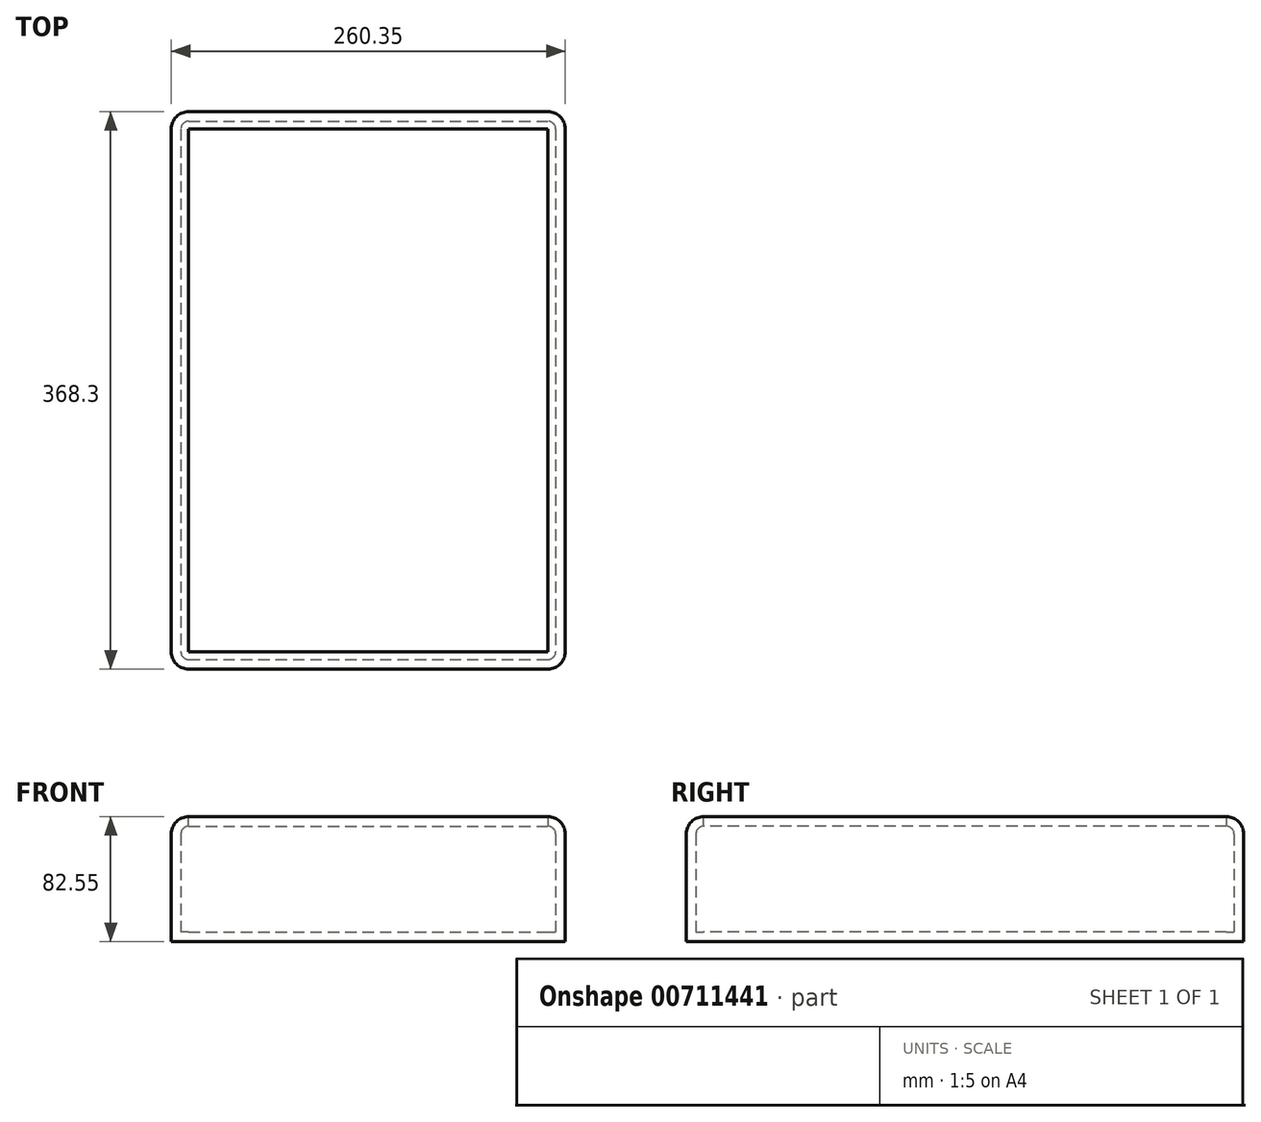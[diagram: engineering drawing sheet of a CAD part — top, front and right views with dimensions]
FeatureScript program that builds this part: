
annotation { "Feature Type Name" : "Feature", "Feature Type Description" : "" }
export const myFeature = defineFeature(function(context is Context, id is Id, definition is map)
    precondition{}
    {
        {
            var Q0;
            Q0=qCreatedBy(makeId("Top.planeOp"),FACE);
            var sketch = newSketch(context, id + "F0", { "sketchPlane" : qUnion([Q0])});
            skLineSegment(sketch, "E0.bottom", {"start": v(-252.64, 180.78) * mm, "end": v(-5, 180.78) * mm});
            skLineSegment(sketch, "E0.top", {"start": v(-252.64, -174.82) * mm, "end": v(-5, -174.82) * mm});
            skLineSegment(sketch, "E0.left", {"start": v(-252.64, 180.78) * mm, "end": v(-252.64, -174.82) * mm});
            skLineSegment(sketch, "E0.right", {"start": v(-5, 180.78) * mm, "end": v(-5, -174.82) * mm});
            skSolve(sketch);
        }
        {
            var Q0;
            Q0=makeQuery(id+"F0.imprint","IMPRINT",FACE,{"disambiguationData":[TD([[makeQuery(id+"F0.imprint","IMPRINT",EDGE,{"derivedFrom":sQuery(id+"F0.wireOp",EDGE,"E0.bottom")}),-1.0]])]});
            extrude(context, id + "F1", {"entities" : qUnion([Q0]), "depth" : 69.85 * mm, "offsetDistance" : 25.4 * mm});
        }
        {
            var Q0;
            Q0=makeQuery(id+"F1.opExtrude","SWEPT_EDGE",EDGE,{"disambiguationData":[OSD([sQuery(id+"F0.wireOp",EDGE,"E0.bottom"),sQuery(id+"F0.wireOp",EDGE,"E0.left")])]});
            var Q1;
            Q1=makeQuery(id+"F1.opExtrude","SWEPT_EDGE",EDGE,{"disambiguationData":[OSD([sQuery(id+"F0.wireOp",EDGE,"E0.bottom"),sQuery(id+"F0.wireOp",EDGE,"E0.right")])]});
            var Q2;
            Q2=makeQuery(id+"F1.opExtrude","SWEPT_EDGE",EDGE,{"disambiguationData":[OSD([sQuery(id+"F0.wireOp",EDGE,"E0.top"),sQuery(id+"F0.wireOp",EDGE,"E0.right")])]});
            var Q3;
            Q3=makeQuery(id+"F1.opExtrude","SWEPT_EDGE",EDGE,{"disambiguationData":[OSD([sQuery(id+"F0.wireOp",EDGE,"E0.top"),sQuery(id+"F0.wireOp",EDGE,"E0.left")])]});
            var Q4;
            Q4=makeQuery(id+"F1.opExtrude","CAP_FACE",FACE,{"disambiguationData":[OSD([sQuery(id+"F0.wireOp",EDGE,"E0.bottom"),sQuery(id+"F0.wireOp",EDGE,"E0.top"),sQuery(id+"F0.wireOp",EDGE,"E0.left"),sQuery(id+"F0.wireOp",EDGE,"E0.right")])],"isStart":false});
            fillet(context, id + "F2", {"entities" : qUnion([Q0, Q1, Q2, Q3, Q4]), "radius" : 5.08 * mm, "tangentPropagation" : true, "allowEdgeOverflow" : false});
        }
        {
            var Q0;
            Q0=makeQuery(id+"F1.opExtrude","CAP_FACE",FACE,{"disambiguationData":[OSD([sQuery(id+"F0.wireOp",EDGE,"E0.bottom"),sQuery(id+"F0.wireOp",EDGE,"E0.top"),sQuery(id+"F0.wireOp",EDGE,"E0.left"),sQuery(id+"F0.wireOp",EDGE,"E0.right")])],"isStart":false});
            shell(context, id + "F3", {"entities" : qUnion([Q0]), "thickness" : 6.35 * mm, "oppositeDirection" : true});
        }
    });
